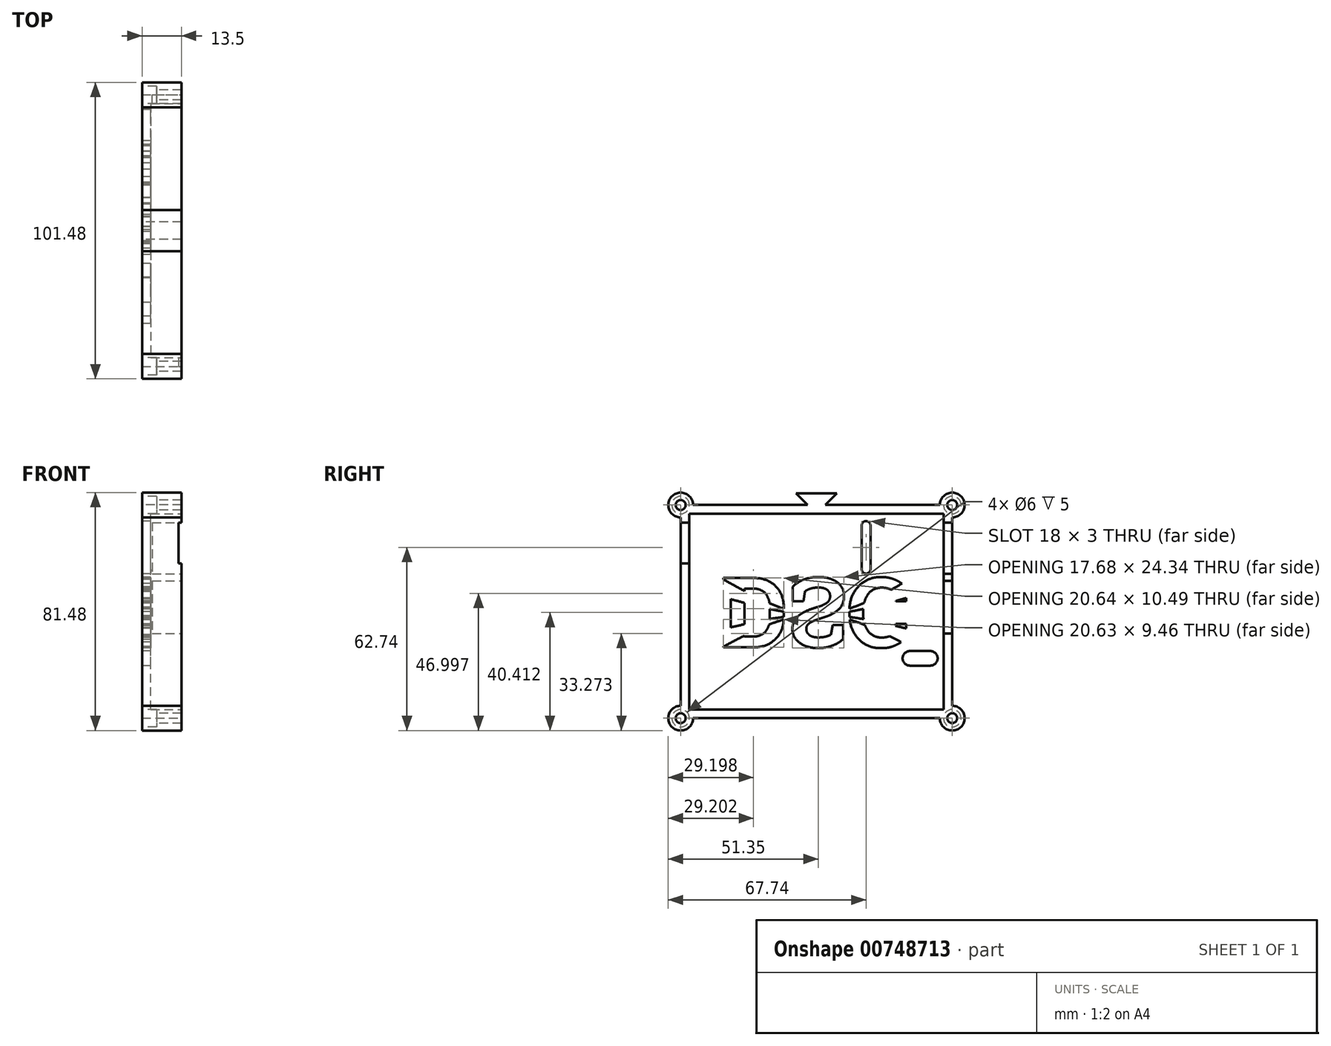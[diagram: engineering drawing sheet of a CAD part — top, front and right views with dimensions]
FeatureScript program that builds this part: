
annotation { "Feature Type Name" : "Feature", "Feature Type Description" : "" }
export const myFeature = defineFeature(function(context is Context, id is Id, definition is map)
    precondition{}
    {
        {
            var Q0;
            Q0=qCreatedBy(makeId("Top.planeOp"),FACE);
            var sketch = newSketch(context, id + "F0", { "sketchPlane" : qUnion([Q0])});
            skLineSegment(sketch, "E0.bottom", {"start": v(-13.5, 46.5) * mm, "end": v(0, 46.5) * mm});
            skLineSegment(sketch, "E0.top", {"start": v(-13.5, -46.5) * mm, "end": v(0, -46.5) * mm});
            skLineSegment(sketch, "E1", {"start": v(-13.5, 46.5) * mm, "end": v(-13.5, -46.5) * mm});
            skLineSegment(sketch, "E2", {"start": v(0, 46.5) * mm, "end": v(0, -46.5) * mm});
            skSolve(sketch);
        }
        {
            var Q0;
            Q0=qSketchRegion(id+"F0",true);
            extrude(context, id + "F1", {"entities" : qUnion([Q0]), "oppositeDirection" : true, "depth" : 73 * mm, "offsetDistance" : 25 * mm});
        }
        {
            var Q0;
            Q0=makeQuery(id+"F1.opExtrude","SWEPT_FACE",FACE,{"disambiguationData":[OSD([sQuery(id+"F0.wireOp",EDGE,"E2")])]});
            shell(context, id + "F2", {"entities" : qUnion([Q0]), "thickness" : 3 * mm});
        }
        {
            var Q0;
            Q0=makeQuery(id+"F1.opExtrude","SWEPT_FACE",FACE,{"disambiguationData":[OSD([sQuery(id+"F0.wireOp",EDGE,"E0.top")])]});
            var sketch = newSketch(context, id + "F3", { "sketchPlane" : qUnion([Q0])});
            skLineSegment(sketch, "E3.bottom", {"start": v(-1, -6) * mm, "end": v(0, -6) * mm});
            skLineSegment(sketch, "E3.top", {"start": v(-1, -20) * mm, "end": v(0, -20) * mm});
            skLineSegment(sketch, "E3.left", {"start": v(-1, -6) * mm, "end": v(-1, -20) * mm});
            skLineSegment(sketch, "E3.right", {"start": v(0, -6) * mm, "end": v(0, -20) * mm});
            skSolve(sketch);
        }
        {
            var Q0;
            Q0 = qSketchRegion(id + "F3", true);
            extrude(context, id + "F4", {"entities" : qUnion([Q0]), "operationType" : NewBodyOperationType.REMOVE, "oppositeDirection" : true, "depth" : 8.5 * mm, "offsetDistance" : 25 * mm});
        }
        {
            var Q0;
            Q0=makeQuery(id+"F1.opExtrude","SWEPT_FACE",FACE,{"disambiguationData":[OSD([sQuery(id+"F0.wireOp",EDGE,"E0.bottom")])]});
            var sketch = newSketch(context, id + "F5", { "sketchPlane" : qUnion([Q0])});
            skLineSegment(sketch, "E4.bottom", {"start": v(10, -6) * mm, "end": v(0, -6) * mm});
            skLineSegment(sketch, "E4.top", {"start": v(10, -23.5) * mm, "end": v(0, -23.5) * mm});
            skLineSegment(sketch, "E4.left", {"start": v(10, -6) * mm, "end": v(10, -23.5) * mm});
            skLineSegment(sketch, "E4.right", {"start": v(0, -6) * mm, "end": v(0, -23.5) * mm});
            skLineSegment(sketch, "E5.bottom", {"start": v(10, -26) * mm, "end": v(0, -26) * mm});
            skLineSegment(sketch, "E5.top", {"start": v(10, -44) * mm, "end": v(0, -44) * mm});
            skLineSegment(sketch, "E5.left", {"start": v(10, -26) * mm, "end": v(10, -44) * mm});
            skLineSegment(sketch, "E5.right", {"start": v(0, -26) * mm, "end": v(0, -44) * mm});
            skSolve(sketch);
        }
        {
            var Q0;
            {var subQ2=sQuery(id+"F0.wireOp",EDGE,"E2");Q0=makeQuery(id+"FEPDLEBXC1Yx2pg_1.boolean.opBoolean","SPLIT",FACE,{"disambiguationData":[TD([makeQuery(id+"F4.boolean.opBoolean","COPY",FACE,{"derivedFrom":makeQuery(id+"F4.opExtrude","SWEPT_FACE",FACE,{"disambiguationData":[OSD([sQuery(id+"F3.wireOp",EDGE,"E3.bottom")])]})})])],"derivedFrom":makeQuery(id+"F1.opExtrude","SWEPT_FACE",FACE,{"disambiguationData":[OSD([subQ2])]})});}
            var sketch = newSketch(context, id + "F6", { "sketchPlane" : qUnion([Q0])});
            skCircle(sketch, "E6", {"center": v(-46.5, 0) * mm, "radius": 4.24 * mm});
            skCircle(sketch, "E7", {"center": v(46.5, 0) * mm, "radius": 4.24 * mm});
            skSolve(sketch);
        }
        {
            var Q0;
            {var subQ2=sQuery(id+"F0.wireOp",EDGE,"E2");Q0=makeQuery(id+"FEPDLEBXC1Yx2pg_1.boolean.opBoolean","SPLIT",FACE,{"disambiguationData":[TD([makeQuery(id+"F4.boolean.opBoolean","COPY",FACE,{"derivedFrom":makeQuery(id+"F4.opExtrude","SWEPT_FACE",FACE,{"disambiguationData":[OSD([sQuery(id+"F3.wireOp",EDGE,"E3.top")])]})})])],"derivedFrom":makeQuery(id+"F1.opExtrude","SWEPT_FACE",FACE,{"disambiguationData":[OSD([subQ2])]})});}
            var sketch = newSketch(context, id + "F7", { "sketchPlane" : qUnion([Q0])});
            skCircle(sketch, "E8", {"center": v(46.5, -73) * mm, "radius": 4.24 * mm});
            skCircle(sketch, "E9", {"center": v(-46.5, -73) * mm, "radius": 4.24 * mm});
            skSolve(sketch);
        }
        {
            var Q0;
            Q0 = qSketchRegion(id + "F6", true);
            extrude(context, id + "F8", {"entities" : qUnion([Q0]), "operationType" : NewBodyOperationType.ADD, "oppositeDirection" : true, "depth" : 13.5 * mm, "offsetDistance" : 25 * mm});
        }
        {
            var Q0;
            Q0 = qSketchRegion(id + "F7", true);
            extrude(context, id + "F9", {"entities" : qUnion([Q0]), "operationType" : NewBodyOperationType.ADD, "oppositeDirection" : true, "depth" : 13.5 * mm, "offsetDistance" : 25 * mm});
        }
        {
            var Q0;
            Q0=makeQuery(id+"F9.boolean.opBoolean","MERGE",FACE,{"derivedFrom":[makeQuery(id+"F8.boolean.opBoolean","MERGE",FACE,{"derivedFrom":[makeQuery(id+"F1.opExtrude","SWEPT_FACE",FACE,{"disambiguationData":[OSD([sQuery(id+"F0.wireOp",EDGE,"E1")])]}),makeQuery(id+"F8.opExtrude","CAP_FACE",FACE,{"disambiguationData":[OSD([sQuery(id+"F6.wireOp",EDGE,"E6")])],"isStart":false}),makeQuery(id+"F8.opExtrude","CAP_FACE",FACE,{"disambiguationData":[OSD([sQuery(id+"F6.wireOp",EDGE,"E7")])],"isStart":false})]}),makeQuery(id+"F9.opExtrude","CAP_FACE",FACE,{"disambiguationData":[OSD([sQuery(id+"F7.wireOp",EDGE,"E8")])],"isStart":false}),makeQuery(id+"F9.opExtrude","CAP_FACE",FACE,{"disambiguationData":[OSD([sQuery(id+"F7.wireOp",EDGE,"E9")])],"isStart":false})]});
            var sketch = newSketch(context, id + "F10", { "sketchPlane" : qUnion([Q0])});
            skPoint(sketch, "E10", {"position": v(46.5, -73) * mm});
            skPoint(sketch, "E11", {"position": v(-46.5, -73) * mm});
            skPoint(sketch, "E12", {"position": v(-46.5, 0) * mm});
            skPoint(sketch, "E13", {"position": v(46.5, 0) * mm});
            skSolve(sketch);
        }
        {
            var Q0;
            Q0=sQuery(id+"F10.wireOp",VERTEX,"E10");
            var Q1;
            Q1=sQuery(id+"F10.wireOp",VERTEX,"E11");
            var Q2;
            Q2=sQuery(id+"F10.wireOp",VERTEX,"E12");
            var Q3;
            Q3=sQuery(id+"F10.wireOp",VERTEX,"E13");
            var Q4;
            Q4=makeQuery(id+"F1.opExtrude","SWEPT_BODY",BODY,{"disambiguationData":[OSD([sQuery(id+"F0.wireOp",EDGE,"E0.bottom"),sQuery(id+"F0.wireOp",EDGE,"E0.top"),sQuery(id+"F0.wireOp",EDGE,"E1"),sQuery(id+"F0.wireOp",EDGE,"E2")])]});
            hole(context, id + "F11", {"style" : HoleStyle.C_BORE, "endStyle" : HoleEndStyle.THROUGH, "holeDiameter" : 3.4 * mm, "cBoreDiameter" : 6 * mm, "cBoreDepth" : 5 * mm, "majorDiameter" : 5 * mm, "isTappedThrough" : true, "tappedDepth" : 12 * mm, "tapClearance" : 3, "startFromSketch" : true, "locations" : qUnion([Q0, Q1, Q2, Q3]), "scope" : qUnion([Q4])});
        }
        {
            var Q0;
            Q0=makeQuery(id+"F9.boolean.opBoolean","MERGE",FACE,{"derivedFrom":[makeQuery(id+"F8.boolean.opBoolean","MERGE",FACE,{"derivedFrom":[makeQuery(id+"F1.opExtrude","SWEPT_FACE",FACE,{"disambiguationData":[OSD([sQuery(id+"F0.wireOp",EDGE,"E1")])]}),makeQuery(id+"F8.opExtrude","CAP_FACE",FACE,{"disambiguationData":[OSD([sQuery(id+"F6.wireOp",EDGE,"E6")])],"isStart":false}),makeQuery(id+"F8.opExtrude","CAP_FACE",FACE,{"disambiguationData":[OSD([sQuery(id+"F6.wireOp",EDGE,"E7")])],"isStart":false})]}),makeQuery(id+"F9.opExtrude","CAP_FACE",FACE,{"disambiguationData":[OSD([sQuery(id+"F7.wireOp",EDGE,"E8")])],"isStart":false}),makeQuery(id+"F9.opExtrude","CAP_FACE",FACE,{"disambiguationData":[OSD([sQuery(id+"F7.wireOp",EDGE,"E9")])],"isStart":false})]});
            var sketch = newSketch(context, id + "F12", { "sketchPlane" : qUnion([Q0])});
            skLineSegment(sketch, "E14.left", {"start": v(-15.5, -22) * mm, "end": v(-15.5, -7) * mm});
            skLineSegment(sketch, "E14.right", {"start": v(-18.5, -22) * mm, "end": v(-18.5, -7) * mm});
            skArc(sketch, "E15", {"start": v(-18.5, -22) * mm, "mid": v(-17, -23.5) * mm, "end": v(-15.5, -22) * mm});
            skArc(sketch, "E16", {"start": v(-15.5, -7) * mm, "mid": v(-17, -5.5) * mm, "end": v(-18.5, -7) * mm});
            skSolve(sketch);
        }
        {
            var Q0;
            Q0 = qSketchRegion(id + "F12", true);
            extrude(context, id + "F13", {"entities" : qUnion([Q0]), "operationType" : NewBodyOperationType.REMOVE, "oppositeDirection" : true, "depth" : 5 * mm, "offsetDistance" : 25 * mm});
        }
        {
            var Q0;
            Q0=makeQuery(id+"F9.boolean.opBoolean","MERGE",FACE,{"derivedFrom":[makeQuery(id+"F8.boolean.opBoolean","MERGE",FACE,{"derivedFrom":[makeQuery(id+"F1.opExtrude","SWEPT_FACE",FACE,{"disambiguationData":[OSD([sQuery(id+"F0.wireOp",EDGE,"E1")])]}),makeQuery(id+"F8.opExtrude","CAP_FACE",FACE,{"disambiguationData":[OSD([sQuery(id+"F6.wireOp",EDGE,"E6")])],"isStart":false}),makeQuery(id+"F8.opExtrude","CAP_FACE",FACE,{"disambiguationData":[OSD([sQuery(id+"F6.wireOp",EDGE,"E7")])],"isStart":false})]}),makeQuery(id+"F9.opExtrude","CAP_FACE",FACE,{"disambiguationData":[OSD([sQuery(id+"F7.wireOp",EDGE,"E8")])],"isStart":false}),makeQuery(id+"F9.opExtrude","CAP_FACE",FACE,{"disambiguationData":[OSD([sQuery(id+"F7.wireOp",EDGE,"E9")])],"isStart":false})]});
            var sketch = newSketch(context, id + "F14", { "sketchPlane" : qUnion([Q0])});
            skText(sketch, "E17", { "text": "DSC", "fontName": "RobotoSlab-Bold.ttf"});
            skLineSegment(sketch, "E18.bottom", {"start": v(35.5, -49) * mm, "end": v(-32.77, -49) * mm});
            skLineSegment(sketch, "E18.top", {"start": v(32.77, -25) * mm, "end": v(-32.77, -25) * mm});
            skLineSegment(sketch, "E18.left", {"start": v(32.77, -49) * mm, "end": v(32.77, -25) * mm});
            skLineSegment(sketch, "E18.right", {"start": v(-32.77, -49) * mm, "end": v(-32.77, -25) * mm});
            skFitSpline(sketch, "E19", {"points": [v(32.77, -49) * mm, v(0, -37.5) * mm, v(-32.77, -49) * mm], "startDerivative": vector(-68.28, 37.5) * mm, "endDerivative": vector(-68.28, -37.5) * mm});
            skFitSpline(sketch, "E20", {"points": [v(-32.77, -25) * mm, v(0, -37.5) * mm, v(32.77, -25) * mm], "startDerivative": vector(68.28, -37.5) * mm, "endDerivative": vector(68.28, 37.5) * mm});
            skLineSegment(sketch, "E21", {"start": v(-32.77, -49) * mm, "end": v(-32.77, -42.75) * mm});
            skFitSpline(sketch, "E22", {"points": [v(-32.77, -42.75) * mm, v(0, -37.5) * mm, v(32.77, -42.75) * mm], "startDerivative": vector(65.55, 15.75) * mm, "endDerivative": vector(65.55, -15.75) * mm});
            skLineSegment(sketch, "E23", {"start": v(-32.77, -25) * mm, "end": v(-32.77, -31.25) * mm});
            skFitSpline(sketch, "E24", {"points": [v(-32.77, -31.25) * mm, v(0, -37.5) * mm, v(32.77, -31.25) * mm], "startDerivative": vector(65.55, -18.75) * mm, "endDerivative": vector(65.55, 18.75) * mm});
            const initialGuessF14  = {"E17": [0.03277, -0.025, -1, 0, 0.024]};
            skSetInitialGuess(sketch, initialGuessF14);
            skSolve(sketch);
        }
        {
            var Q0;
            {var subQ0=sQuery(id+"F14.wireOp",EDGE,"E17.sketch_text.stroke-63");Q0=makeQuery(id+"F14.imprint","IMPRINT",FACE,{"disambiguationData":[TD([[makeQuery(id+"F14.imprint","IMPRINT",EDGE,{"derivedFrom":subQ0}),-1.0]])]});}
            var Q1;
            {var subQ16=sQuery(id+"F14.wireOp",EDGE,"E17.sketch_text.stroke-59");Q1=makeQuery(id+"F14.imprint","IMPRINT",FACE,{"disambiguationData":[TD([[makeQuery(id+"F14.imprint","IMPRINT",EDGE,{"derivedFrom":subQ16}),-1.0]])]});}
            var Q2;
            {var subQ5=sQuery(id+"F14.wireOp",EDGE,"E17.sketch_text.stroke-57");Q2=makeQuery(id+"F14.imprint","IMPRINT",FACE,{"disambiguationData":[TD([[makeQuery(id+"F14.imprint","IMPRINT",EDGE,{"derivedFrom":subQ5}),-1.0]])]});}
            var Q3;
            {var subQ15=sQuery(id+"F14.wireOp",EDGE,"E17.sketch_text.stroke-54");Q3=makeQuery(id+"F14.imprint","IMPRINT",FACE,{"disambiguationData":[TD([[makeQuery(id+"F14.imprint","IMPRINT",EDGE,{"derivedFrom":subQ15}),-1.0]])]});}
            var Q4;
            {var subQ0=sQuery(id+"F14.wireOp",EDGE,"E17.sketch_text.stroke-51");Q4=makeQuery(id+"F14.imprint","IMPRINT",FACE,{"disambiguationData":[TD([[makeQuery(id+"F14.imprint","IMPRINT",EDGE,{"derivedFrom":subQ0}),-1.0]])]});}
            var Q5;
            {var subQ4=sQuery(id+"F14.wireOp",EDGE,"E17.sketch_text.stroke-30");Q5=makeQuery(id+"F14.imprint","IMPRINT",FACE,{"disambiguationData":[TD([[makeQuery(id+"F14.imprint","IMPRINT",EDGE,{"derivedFrom":subQ4}),-1.0]])]});}
            var Q6;
            Q6=makeQuery(id+"F14.imprint","IMPRINT",FACE,{"disambiguationData":[TD([[makeQuery(id+"F14.imprint","IMPRINT",EDGE,{"derivedFrom":sQuery(id+"F14.wireOp",EDGE,"E17.sketch_text.stroke-21")}),-1.0]])]});
            var Q7;
            {var subQ0=sQuery(id+"F14.wireOp",EDGE,"E24");var subQ1=sQuery(id+"F14.wireOp",EDGE,"E17.sketch_text.stroke-29");var subQ2=makeQuery(id+"F14.imprint","INTERSECT",VERTEX,{"derivedFrom":[subQ1,subQ0]});Q7=makeQuery(id+"F14.imprint","IMPRINT",FACE,{"disambiguationData":[TD([[makeQuery(id+"F14.imprint","IMPRINT",EDGE,{"disambiguationData":[TD([[subQ2,-1.0]])],"derivedFrom":subQ1}),-1.0]])]});}
            var Q8;
            {var subQ0=sQuery(id+"F14.wireOp",EDGE,"E19");var subQ1=sQuery(id+"F14.wireOp",EDGE,"E17.sketch_text.stroke-29");var subQ2=makeQuery(id+"F14.imprint","INTERSECT",VERTEX,{"derivedFrom":[subQ1,subQ0]});Q8=makeQuery(id+"F14.imprint","IMPRINT",FACE,{"disambiguationData":[TD([[makeQuery(id+"F14.imprint","IMPRINT",EDGE,{"disambiguationData":[TD([[subQ2,-1.0]])],"derivedFrom":subQ1}),-1.0]])]});}
            var Q9;
            {var subQ0=sQuery(id+"F14.wireOp",EDGE,"E22");var subQ1=sQuery(id+"F14.wireOp",EDGE,"E17.sketch_text.stroke-29");var subQ2=makeQuery(id+"F14.imprint","INTERSECT",VERTEX,{"derivedFrom":[subQ1,subQ0]});Q9=makeQuery(id+"F14.imprint","IMPRINT",FACE,{"disambiguationData":[TD([[makeQuery(id+"F14.imprint","IMPRINT",EDGE,{"disambiguationData":[TD([[subQ2,-1.0]])],"derivedFrom":subQ1}),-1.0]])]});}
            var Q10;
            {var subQ0=sQuery(id+"F14.wireOp",EDGE,"E20");var subQ1=sQuery(id+"F14.wireOp",EDGE,"E17.sketch_text.stroke-44");var subQ2=makeQuery(id+"F14.imprint","INTERSECT",VERTEX,{"derivedFrom":[subQ1,subQ0]});Q10=makeQuery(id+"F14.imprint","IMPRINT",FACE,{"disambiguationData":[TD([[makeQuery(id+"F14.imprint","IMPRINT",EDGE,{"disambiguationData":[TD([[subQ2,-1.0]])],"derivedFrom":subQ1}),-1.0]])]});}
            var Q11;
            {var subQ0=sQuery(id+"F14.wireOp",EDGE,"E24");var subQ1=sQuery(id+"F14.wireOp",EDGE,"E17.sketch_text.stroke-44");var subQ2=makeQuery(id+"F14.imprint","INTERSECT",VERTEX,{"derivedFrom":[subQ1,subQ0]});Q11=makeQuery(id+"F14.imprint","IMPRINT",FACE,{"disambiguationData":[TD([[makeQuery(id+"F14.imprint","IMPRINT",EDGE,{"disambiguationData":[TD([[subQ2,-1.0]])],"derivedFrom":subQ1}),-1.0]])]});}
            var Q12;
            {var subQ0=sQuery(id+"F14.wireOp",EDGE,"E17.sketch_text.stroke-45");var subQ1=sQuery(id+"F14.wireOp",EDGE,"E17.sketch_text.stroke-44");var subQ2=makeQuery(id+"F14.imprint","INTERSECT",VERTEX,{"derivedFrom":[subQ1,subQ0]});Q12=makeQuery(id+"F14.imprint","IMPRINT",FACE,{"disambiguationData":[TD([[makeQuery(id+"F14.imprint","IMPRINT",EDGE,{"disambiguationData":[TD([[subQ2,1.0]])],"derivedFrom":subQ1}),-1.0]])]});}
            var Q13;
            {var subQ9=sQuery(id+"F14.wireOp",EDGE,"E17.sketch_text.stroke-3");Q13=makeQuery(id+"F14.imprint","IMPRINT",FACE,{"disambiguationData":[TD([[makeQuery(id+"F14.imprint","IMPRINT",EDGE,{"derivedFrom":subQ9}),-1.0]])]});}
            var Q14;
            {var subQ0=sQuery(id+"F14.wireOp",EDGE,"E22");var subQ1=sQuery(id+"F14.wireOp",EDGE,"E17.sketch_text.stroke-2");var subQ2=makeQuery(id+"F14.imprint","INTERSECT",VERTEX,{"derivedFrom":[subQ1,subQ0]});Q14=makeQuery(id+"F14.imprint","IMPRINT",FACE,{"disambiguationData":[TD([[makeQuery(id+"F14.imprint","IMPRINT",EDGE,{"disambiguationData":[TD([[subQ2,-1.0]])],"derivedFrom":subQ1}),-1.0]])]});}
            var Q15;
            {var subQ7=sQuery(id+"F14.wireOp",EDGE,"E17.sketch_text.stroke-0");Q15=makeQuery(id+"F14.imprint","IMPRINT",FACE,{"disambiguationData":[TD([[makeQuery(id+"F14.imprint","IMPRINT",EDGE,{"derivedFrom":subQ7}),-1.0]])]});}
            var Q16;
            {var subQ0=sQuery(id+"F14.wireOp",EDGE,"E24");var subQ1=sQuery(id+"F14.wireOp",EDGE,"E17.sketch_text.stroke-8");var subQ2=makeQuery(id+"F14.imprint","INTERSECT",VERTEX,{"derivedFrom":[subQ1,subQ0]});Q16=makeQuery(id+"F14.imprint","IMPRINT",FACE,{"disambiguationData":[TD([[makeQuery(id+"F14.imprint","IMPRINT",EDGE,{"disambiguationData":[TD([[subQ2,-1.0]])],"derivedFrom":subQ1}),-1.0]])]});}
            var Q17;
            {var subQ0=sQuery(id+"F14.wireOp",EDGE,"E17.sketch_text.stroke-33");var subQ1=sQuery(id+"F14.wireOp",EDGE,"E17.sketch_text.stroke-32");var subQ2=makeQuery(id+"F14.imprint","INTERSECT",VERTEX,{"derivedFrom":[subQ1,subQ0]});Q17=makeQuery(id+"F14.imprint","IMPRINT",FACE,{"disambiguationData":[TD([[makeQuery(id+"F14.imprint","IMPRINT",EDGE,{"disambiguationData":[TD([[subQ2,1.0]])],"derivedFrom":subQ1}),-1.0]])]});}
            var Q18;
            {var subQ0=sQuery(id+"F14.wireOp",EDGE,"E17.sketch_text.stroke-67");var subQ1=sQuery(id+"F14.wireOp",EDGE,"E17.sketch_text.stroke-66");var subQ2=makeQuery(id+"F14.imprint","INTERSECT",VERTEX,{"derivedFrom":[subQ1,subQ0]});Q18=makeQuery(id+"F14.imprint","IMPRINT",FACE,{"disambiguationData":[TD([[makeQuery(id+"F14.imprint","IMPRINT",EDGE,{"disambiguationData":[TD([[subQ2,1.0]])],"derivedFrom":subQ1}),-1.0]])]});}
            extrude(context, id + "F15", {"entities" : qUnion([Q0, Q1, Q2, Q3, Q4, Q5, Q6, Q7, Q8, Q9, Q10, Q11, Q12, Q13, Q14, Q15, Q16, Q17, Q18]), "operationType" : NewBodyOperationType.REMOVE, "oppositeDirection" : true, "depth" : 5 * mm, "offsetDistance" : 25 * mm});
        }
        {
            var Q0;
            Q0 = qSketchRegion(id + "F5", true);
            extrude(context, id + "F16", {"entities" : qUnion([Q0]), "operationType" : NewBodyOperationType.REMOVE, "oppositeDirection" : true, "depth" : 5 * mm, "offsetDistance" : 25 * mm});
        }
        {
            var Q0;
            Q0=makeQuery(id+"F9.boolean.opBoolean","MERGE",FACE,{"derivedFrom":[makeQuery(id+"F8.boolean.opBoolean","MERGE",FACE,{"derivedFrom":[makeQuery(id+"F1.opExtrude","SWEPT_FACE",FACE,{"disambiguationData":[OSD([sQuery(id+"F0.wireOp",EDGE,"E1")])]}),makeQuery(id+"F8.opExtrude","CAP_FACE",FACE,{"disambiguationData":[OSD([sQuery(id+"F6.wireOp",EDGE,"E6")])],"isStart":false}),makeQuery(id+"F8.opExtrude","CAP_FACE",FACE,{"disambiguationData":[OSD([sQuery(id+"F6.wireOp",EDGE,"E7")])],"isStart":false})]}),makeQuery(id+"F9.opExtrude","CAP_FACE",FACE,{"disambiguationData":[OSD([sQuery(id+"F7.wireOp",EDGE,"E8")])],"isStart":false}),makeQuery(id+"F9.opExtrude","CAP_FACE",FACE,{"disambiguationData":[OSD([sQuery(id+"F7.wireOp",EDGE,"E9")])],"isStart":false})]});
            var sketch = newSketch(context, id + "F17", { "sketchPlane" : qUnion([Q0])});
            skLineSegment(sketch, "E25", {"start": v(-3, 0) * mm, "end": v(-7, 4) * mm});
            skLineSegment(sketch, "E26", {"start": v(-7, 4) * mm, "end": v(7, 4) * mm});
            skLineSegment(sketch, "E27", {"start": v(7, 4) * mm, "end": v(3, 0) * mm});
            skSolve(sketch);
        }
        {
            var Q0;
            {var subQ0=sQuery(id+"F17.wireOp",EDGE,"E25");Q0=makeQuery(id+"F17.imprint","IMPRINT",FACE,{"disambiguationData":[TD([[makeQuery(id+"F17.imprint","IMPRINT",EDGE,{"derivedFrom":subQ0}),-1.0]])]});}
            extrude(context, id + "F18", {"entities" : qUnion([Q0]), "operationType" : NewBodyOperationType.ADD, "oppositeDirection" : true, "depth" : 13.5 * mm, "offsetDistance" : 25 * mm});
        }
        {
            var Q0;
            {var subQ0=sQuery(id+"F0.wireOp",EDGE,"E1");Q0=makeQuery(id+"F18.boolean.opBoolean","MERGE",FACE,{"derivedFrom":[makeQuery(id+"F9.boolean.opBoolean","MERGE",FACE,{"derivedFrom":[makeQuery(id+"F8.boolean.opBoolean","MERGE",FACE,{"derivedFrom":[makeQuery(id+"F1.opExtrude","SWEPT_FACE",FACE,{"disambiguationData":[OSD([subQ0])]}),makeQuery(id+"F8.opExtrude","CAP_FACE",FACE,{"disambiguationData":[OSD([sQuery(id+"F6.wireOp",EDGE,"E6")])],"isStart":false}),makeQuery(id+"F8.opExtrude","CAP_FACE",FACE,{"disambiguationData":[OSD([sQuery(id+"F6.wireOp",EDGE,"E7")])],"isStart":false})]}),makeQuery(id+"F9.opExtrude","CAP_FACE",FACE,{"disambiguationData":[OSD([sQuery(id+"F7.wireOp",EDGE,"E8")])],"isStart":false}),makeQuery(id+"F9.opExtrude","CAP_FACE",FACE,{"disambiguationData":[OSD([sQuery(id+"F7.wireOp",EDGE,"E9")])],"isStart":false})]}),makeQuery(id+"F18.opExtrude","CAP_FACE",FACE,{"disambiguationData":[OSD([subQ0,sQuery(id+"F17.wireOp",EDGE,"E25"),sQuery(id+"F17.wireOp",EDGE,"E26"),sQuery(id+"F17.wireOp",EDGE,"E27")])],"isStart":true})]});}
            var sketch = newSketch(context, id + "F19", { "sketchPlane" : qUnion([Q0])});
            skLineSegment(sketch, "E28.bottom", {"start": v(-32, -55) * mm, "end": v(-39, -55) * mm});
            skLineSegment(sketch, "E28.top", {"start": v(-32, -50) * mm, "end": v(-39, -50) * mm});
            skArc(sketch, "E29", {"start": v(-32, -55) * mm, "mid": v(-29.5, -52.5) * mm, "end": v(-32, -50) * mm});
            skArc(sketch, "E30", {"start": v(-39, -50) * mm, "mid": v(-41.5, -52.5) * mm, "end": v(-39, -55) * mm});
            skSolve(sketch);
        }
        {
            var Q0;
            Q0=makeQuery(id+"F19.imprint","IMPRINT",FACE,{"disambiguationData":[TD([[makeQuery(id+"F19.imprint","IMPRINT",EDGE,{"derivedFrom":sQuery(id+"F19.wireOp",EDGE,"E28.bottom")}),-1.0]])]});
            extrude(context, id + "F20", {"entities" : qUnion([Q0]), "operationType" : NewBodyOperationType.REMOVE, "oppositeDirection" : true, "depth" : 5 * mm, "offsetDistance" : 25 * mm});
        }
    });
